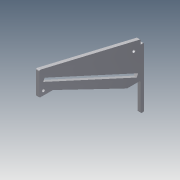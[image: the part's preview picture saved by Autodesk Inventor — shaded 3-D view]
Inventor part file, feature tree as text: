
AUTODESK INVENTOR PART (.ipt)
format: ipt  version: 2014 (Build 180170000, 170)  size: 137,216 bytes
history: native  units: mm
features: extrude x4, sketch x4, fillet x1
ambient origin geometry x8: Origin, YZ Plane, XZ Plane, XY Plane, X Axis, Y Axis, Z Axis, Center Point
bodies: Solid1 (feature_tree)
feature tree (9):
  extrude  "Extrusion1"  Depth=65.0mm
  extrude  "Extrusion3"  Depth=6.0mm TaperAngle=0.0deg
  extrude  "Extrusion4"  Depth=25.0mm
  extrude  "Extrusion5"  Depth=6.0mm
  fillet  "Fillet1"  Radius=6.0mm
  sketch  "Sketch1"  dims[d0=25.0mm d1=65.0mm]
  sketch  "Sketch3"  dims[d2=185.0mm d3=6.0mm d4=0.0mm]
  sketch  "Sketch4"  dims[d10=25.0mm d11=25.0mm]
  sketch  "Sketch5"  dims[d12=8.1mm d14=6.0mm d15=6.0mm d16=0.0mm d17=25.0mm d20=25.0mm d21=108.8mm d23=185.0mm d24=85.0mm d28=8.0mm d29=8.0mm d30=6.0mm d31=0.0mm d32=6.0mm d33=2.0mm d34=12.5mm d35=12.5mm d36=5.4mm d37=5.4mm d38=8.0mm d39=8.0mm d40=6.0mm d41=0.0mm]
